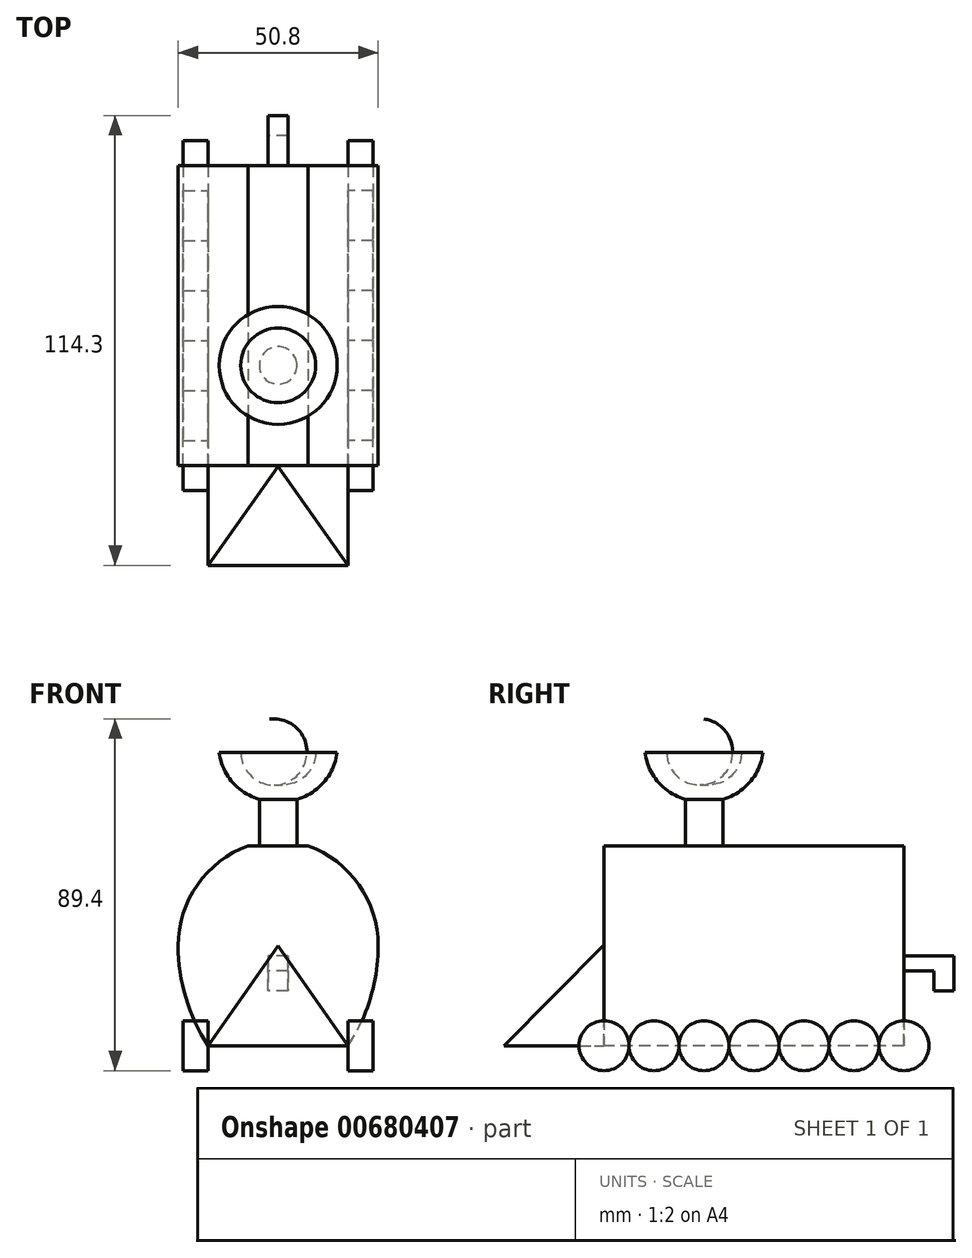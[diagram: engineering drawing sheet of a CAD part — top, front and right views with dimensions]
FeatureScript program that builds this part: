
annotation { "Feature Type Name" : "Feature", "Feature Type Description" : "" }
export const myFeature = defineFeature(function(context is Context, id is Id, definition is map)
    precondition{}
    {
        {
            var Q0;
            Q0=qCreatedBy(makeId("Front.planeOp"),FACE);
            var sketch = newSketch(context, id + "F0", { "sketchPlane" : qUnion([Q0])});
            skLineSegment(sketch, "E0", {"start": v(0, 0) * mm, "end": v(0, 50.8) * mm});
            skLineSegment(sketch, "E1", {"start": v(0, 50.8) * mm, "end": v(50.8, 50.8) * mm});
            skLineSegment(sketch, "E2", {"start": v(50.8, 50.8) * mm, "end": v(50.8, 0) * mm});
            skLineSegment(sketch, "E3", {"start": v(50.8, 0) * mm, "end": v(0, 0) * mm});
            skSolve(sketch);
        }
        {
            var Q0;
            Q0=makeQuery(id+"F0.imprint","IMPRINT",FACE,{"disambiguationData":[TD([[makeQuery(id+"F0.imprint","IMPRINT",EDGE,{"derivedFrom":sQuery(id+"F0.wireOp",EDGE,"E0")}),-1.0]])]});
            extrude(context, id + "F1", {"entities" : qUnion([Q0]), "depth" : 76.2 * mm});
        }
        {
            var Q0;
            Q0=qCreatedBy(makeId("Right.planeOp"),FACE);
            cPlane(context, id + "F2", {"entities" : qUnion([Q0]), "cplaneType" : CPlaneType.OFFSET, "offset" : 50.8 * mm, "width" : 152.4 * mm, "height" : 152.4 * mm});
        }
        {
            var Q0;
            Q0=qCreatedBy(makeId("Front.planeOp"),FACE);
            cPlane(context, id + "F3", {"entities" : qUnion([Q0]), "cplaneType" : CPlaneType.OFFSET, "offset" : 76.2 * mm, "width" : 152.4 * mm, "height" : 152.4 * mm});
        }
        {
            var Q0;
            Q0=qCreatedBy(id+"F3.planeOp",FACE);
            var sketch = newSketch(context, id + "F4", { "sketchPlane" : qUnion([Q0])});
            skLineSegment(sketch, "E4", {"start": v(0, 0) * mm, "end": v(0, 50.8) * mm});
            skLineSegment(sketch, "E5", {"start": v(0, 50.8) * mm, "end": v(50.8, 50.8) * mm});
            skLineSegment(sketch, "E6", {"start": v(50.8, 50.8) * mm, "end": v(50.8, 0) * mm});
            skLineSegment(sketch, "E7", {"start": v(50.8, 0) * mm, "end": v(0, 0) * mm});
            skLineSegment(sketch, "E8", {"start": v(43.18, 0) * mm, "end": v(25.4, 25.4) * mm});
            skPoint(sketch, "E8.endSnap0", {"position": v(25.4, 50.8) * mm});
            skPoint(sketch, "E8.endSnap1", {"position": v(0, 25.4) * mm});
            skLineSegment(sketch, "E9", {"start": v(25.4, 25.4) * mm, "end": v(7.62, 0) * mm});
            skSolve(sketch);
        }
        {
            var Q0;
            {var subQ0=sQuery(id+"F4.wireOp",EDGE,"E8");Q0=makeQuery(id+"F4.imprint","IMPRINT",FACE,{"disambiguationData":[TD([[makeQuery(id+"F4.imprint","IMPRINT",EDGE,{"derivedFrom":subQ0}),1.0]])]});}
            extrude(context, id + "F5", {"entities" : qUnion([Q0]), "operationType" : NewBodyOperationType.ADD, "depth" : 25.4 * mm});
        }
        {
            var Q0;
            Q0=qCreatedBy(makeId("Right.planeOp"),FACE);
            var sketch = newSketch(context, id + "F6", { "sketchPlane" : qUnion([Q0])});
            skLineSegment(sketch, "E10", {"start": v(-101.6, 0) * mm, "end": v(-76.53, 25.4) * mm});
            skLineSegment(sketch, "E11", {"start": v(-76.53, 25.4) * mm, "end": v(-101.93, 25.4) * mm});
            skLineSegment(sketch, "E12", {"start": v(-101.93, 25.4) * mm, "end": v(-101.6, 0) * mm});
            skSolve(sketch);
        }
        {
            var Q0;
            Q0=makeQuery(id+"F6.imprint","IMPRINT",FACE,{"disambiguationData":[TD([[makeQuery(id+"F6.imprint","IMPRINT",EDGE,{"derivedFrom":sQuery(id+"F6.wireOp",EDGE,"E10")}),1.0]])]});
            extrude(context, id + "F7", {"entities" : qUnion([Q0]), "operationType" : NewBodyOperationType.REMOVE, "depth" : 50.8 * mm});
        }
        {
            var Q0;
            Q0=qCreatedBy(makeId("Right.planeOp"),FACE);
            cPlane(context, id + "F8", {"entities" : qUnion([Q0]), "cplaneType" : CPlaneType.OFFSET, "offset" : 25.4 * mm, "width" : 152.4 * mm, "height" : 152.4 * mm});
        }
        {
            var Q0;
            Q0=qCreatedBy(id+"F8.planeOp",FACE);
            var sketch = newSketch(context, id + "F9", { "sketchPlane" : qUnion([Q0])});
            skLineSegment(sketch, "E13", {"start": v(-50.8, 50.8) * mm, "end": v(-50.8, 66.3) * mm});
            skArc(sketch, "E14", {"start": v(-60.3, 74.53) * mm, "mid": v(-57.4, 68.28) * mm, "end": v(-50.8, 66.3) * mm});
            skLineSegment(sketch, "E15", {"start": v(-60.3, 74.53) * mm, "end": v(-65.8, 74.53) * mm});
            skArc(sketch, "E16", {"start": v(-65.8, 74.53) * mm, "mid": v(-62.47, 67.01) * mm, "end": v(-55.57, 62.56) * mm});
            skLineSegment(sketch, "E17", {"start": v(-50.8, 50.8) * mm, "end": v(-55.57, 50.8) * mm});
            skLineSegment(sketch, "E18", {"start": v(-55.57, 50.8) * mm, "end": v(-55.57, 62.56) * mm});
            skSolve(sketch);
        }
        {
            var Q0;
            Q0=qSketchRegion(id+"F9",true);
            var Q1;
            Q1=sQuery(id+"F9.wireOp",EDGE,"E13");
            revolve(context, id + "F10", {"operationType" : NewBodyOperationType.ADD, "entities" : qUnion([Q0]), "axis" : qUnion([Q1]), "revolveType" : RevolveType.FULL});
        }
        {
            var Q0;
            Q0=makeQuery(id+"F1.opExtrude","CAP_FACE",FACE,{"disambiguationData":[OSD([sQuery(id+"F0.wireOp",EDGE,"E0"),sQuery(id+"F0.wireOp",EDGE,"E1"),sQuery(id+"F0.wireOp",EDGE,"E2"),sQuery(id+"F0.wireOp",EDGE,"E3")])],"isStart":false});
            var sketch = newSketch(context, id + "F11", { "sketchPlane" : qUnion([Q0])});
            skArc(sketch, "E19", {"start": v(17.78, 50.8) * mm, "mid": v(4.89, 40.9) * mm, "end": v(0, 25.4) * mm});
            skArc(sketch, "E20", {"start": v(50.8, 25.4) * mm, "mid": v(45.91, 40.9) * mm, "end": v(33.02, 50.8) * mm});
            skLineSegment(sketch, "E21", {"start": v(0, 25.4) * mm, "end": v(0, 50.8) * mm});
            skLineSegment(sketch, "E22", {"start": v(0, 50.8) * mm, "end": v(17.78, 50.8) * mm});
            skLineSegment(sketch, "E23", {"start": v(33.02, 50.8) * mm, "end": v(50.8, 50.8) * mm});
            skLineSegment(sketch, "E24", {"start": v(50.8, 50.8) * mm, "end": v(50.8, 25.4) * mm});
            skArc(sketch, "E25", {"start": v(0, 25.4) * mm, "mid": v(1.95, 12.14) * mm, "end": v(7.62, 0) * mm});
            skArc(sketch, "E26", {"start": v(43.18, 0) * mm, "mid": v(48.85, 12.14) * mm, "end": v(50.8, 25.4) * mm});
            skLineSegment(sketch, "E27", {"start": v(0, 25.4) * mm, "end": v(0, 0) * mm});
            skLineSegment(sketch, "E28", {"start": v(0, 0) * mm, "end": v(7.62, 0) * mm});
            skLineSegment(sketch, "E29", {"start": v(43.18, 0) * mm, "end": v(50.8, 0) * mm});
            skLineSegment(sketch, "E30", {"start": v(50.8, 0) * mm, "end": v(50.8, 25.4) * mm});
            skSolve(sketch);
        }
        {
            var Q0;
            Q0=makeQuery(id+"F11.imprint","IMPRINT",FACE,{"disambiguationData":[TD([[makeQuery(id+"F11.imprint","IMPRINT",EDGE,{"derivedFrom":sQuery(id+"F11.wireOp",EDGE,"E20")}),-1.0]])]});
            var Q1;
            Q1=makeQuery(id+"F11.imprint","IMPRINT",FACE,{"disambiguationData":[TD([[makeQuery(id+"F11.imprint","IMPRINT",EDGE,{"derivedFrom":sQuery(id+"F11.wireOp",EDGE,"E19")}),-1.0]])]});
            var Q2;
            Q2=makeQuery(id+"F11.imprint","IMPRINT",FACE,{"disambiguationData":[TD([[makeQuery(id+"F11.imprint","IMPRINT",EDGE,{"derivedFrom":sQuery(id+"F11.wireOp",EDGE,"E25")}),-1.0]])]});
            var Q3;
            Q3=makeQuery(id+"F11.imprint","IMPRINT",FACE,{"disambiguationData":[TD([[makeQuery(id+"F11.imprint","IMPRINT",EDGE,{"derivedFrom":sQuery(id+"F11.wireOp",EDGE,"E26")}),-1.0]])]});
            extrude(context, id + "F12", {"entities" : qUnion([Q0, Q1, Q2, Q3]), "operationType" : NewBodyOperationType.REMOVE, "oppositeDirection" : true, "depth" : 76.2 * mm});
        }
        {
            var Q0;
            Q0=qCreatedBy(makeId("Right.planeOp"),FACE);
            cPlane(context, id + "F13", {"entities" : qUnion([Q0]), "cplaneType" : CPlaneType.OFFSET, "offset" : 7.62 * mm, "width" : 152.4 * mm, "height" : 152.4 * mm});
        }
        {
            var Q0;
            Q0=qCreatedBy(id+"F13.planeOp",FACE);
            var sketch = newSketch(context, id + "F14", { "sketchPlane" : qUnion([Q0])});
            skCircle(sketch, "E31", {"center": v(-12.7, 0) * mm, "radius": 6.35 * mm});
            skCircle(sketch, "E32", {"center": v(-25.4, 0) * mm, "radius": 6.35 * mm});
            skCircle(sketch, "E33", {"center": v(-38.1, 0) * mm, "radius": 6.35 * mm});
            skCircle(sketch, "E34", {"center": v(-50.8, 0) * mm, "radius": 6.35 * mm});
            skCircle(sketch, "E35", {"center": v(-63.5, 0) * mm, "radius": 6.35 * mm});
            skCircle(sketch, "E36", {"center": v(0, 0) * mm, "radius": 6.35 * mm});
            skCircle(sketch, "E37", {"center": v(-76.2, 0) * mm, "radius": 6.35 * mm});
            skSolve(sketch);
        }
        {
            var Q0;
            Q0=qSketchRegion(id+"F14",true);
            extrude(context, id + "F15", {"entities" : qUnion([Q0]), "oppositeDirection" : true, "depth" : 6.35 * mm});
        }
        {
            var Q0;
            Q0=qCreatedBy(id+"F2.planeOp",FACE);
            cPlane(context, id + "F16", {"entities" : qUnion([Q0]), "cplaneType" : CPlaneType.OFFSET, "offset" : 7.62 * mm, "oppositeDirection" : true, "width" : 152.4 * mm, "height" : 152.4 * mm});
        }
        {
            var Q0;
            Q0=qCreatedBy(id+"F16.planeOp",FACE);
            var sketch = newSketch(context, id + "F17", { "sketchPlane" : qUnion([Q0])});
            skCircle(sketch, "E38", {"center": v(-76.2, 0) * mm, "radius": 6.35 * mm});
            skCircle(sketch, "E39", {"center": v(-63.5, 0) * mm, "radius": 6.35 * mm});
            skCircle(sketch, "E40", {"center": v(-50.8, 0) * mm, "radius": 6.35 * mm});
            skCircle(sketch, "E41", {"center": v(-38.1, 0) * mm, "radius": 6.35 * mm});
            skCircle(sketch, "E42", {"center": v(-25.4, 0) * mm, "radius": 6.35 * mm});
            skCircle(sketch, "E43", {"center": v(-12.7, 0) * mm, "radius": 6.35 * mm});
            skCircle(sketch, "E44", {"center": v(0, 0) * mm, "radius": 6.35 * mm});
            skSolve(sketch);
        }
        {
            var Q0;
            Q0=qSketchRegion(id+"F17",true);
            extrude(context, id + "F18", {"entities" : qUnion([Q0]), "depth" : 6.35 * mm});
        }
        {
            var Q0;
            Q0=qCreatedBy(id+"F8.planeOp",FACE);
            var sketch = newSketch(context, id + "F19", { "sketchPlane" : qUnion([Q0])});
            skLineSegment(sketch, "E45", {"start": v(0, 19.05) * mm, "end": v(7.62, 19.05) * mm});
            skLineSegment(sketch, "E46", {"start": v(7.62, 19.05) * mm, "end": v(7.62, 13.97) * mm});
            skLineSegment(sketch, "E47", {"start": v(7.62, 13.97) * mm, "end": v(12.7, 13.97) * mm});
            skLineSegment(sketch, "E48", {"start": v(12.7, 13.97) * mm, "end": v(12.7, 22.86) * mm});
            skLineSegment(sketch, "E49", {"start": v(12.7, 22.86) * mm, "end": v(0, 22.86) * mm});
            skLineSegment(sketch, "E50", {"start": v(0, 22.86) * mm, "end": v(0, 19.05) * mm});
            skSolve(sketch);
        }
        {
            var Q0;
            Q0=makeQuery(id+"F19.imprint","IMPRINT",FACE,{"disambiguationData":[TD([[makeQuery(id+"F19.imprint","IMPRINT",EDGE,{"derivedFrom":sQuery(id+"F19.wireOp",EDGE,"E45")}),1.0]])]});
            extrude(context, id + "F20", {"entities" : qUnion([Q0]), "operationType" : NewBodyOperationType.ADD, "depth" : 2.54 * mm});
        }
        {
            var Q0;
            Q0=qSketchRegion(id+"F19",true);
            extrude(context, id + "F21", {"entities" : qUnion([Q0]), "operationType" : NewBodyOperationType.ADD, "oppositeDirection" : true, "depth" : 2.54 * mm});
        }
    });
